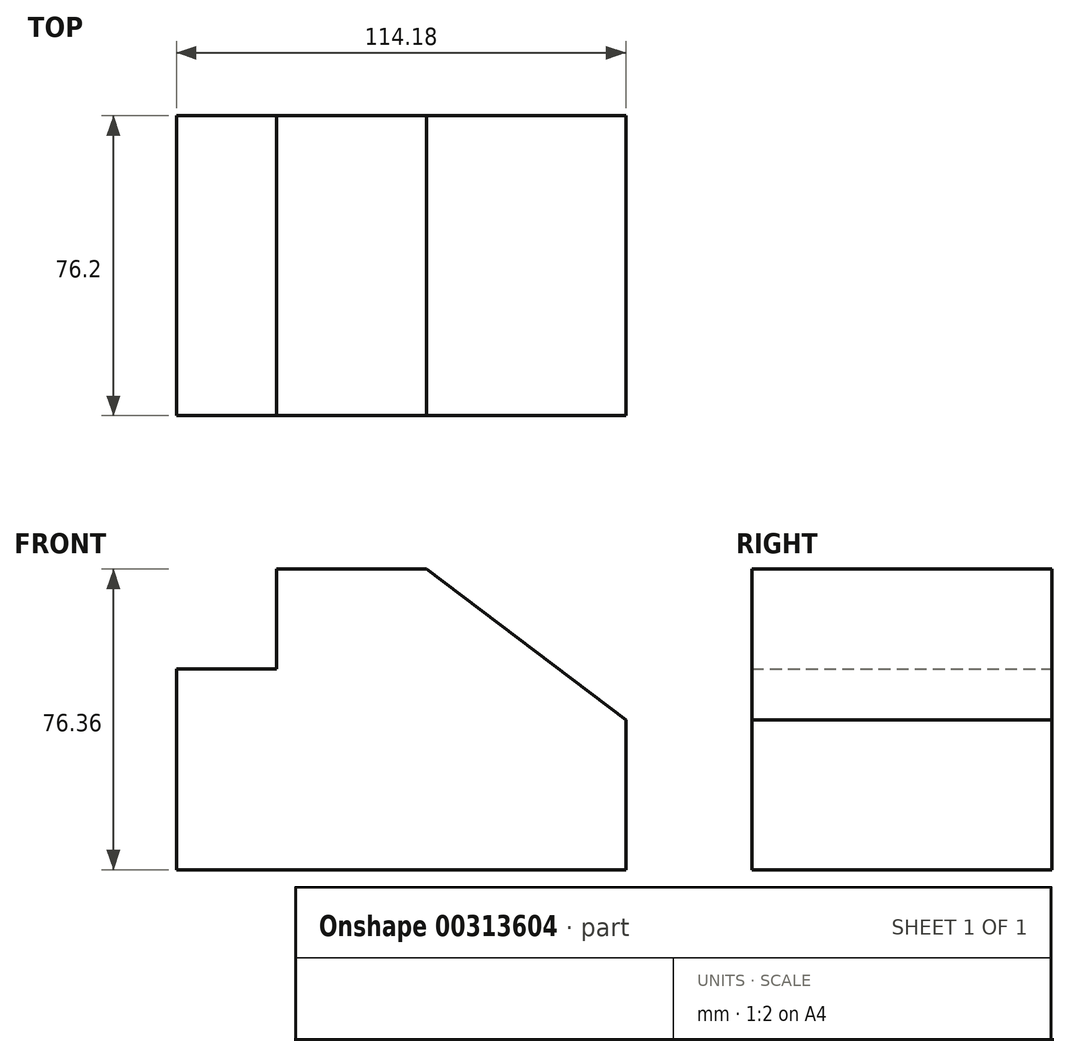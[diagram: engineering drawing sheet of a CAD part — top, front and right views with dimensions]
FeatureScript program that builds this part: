
annotation { "Feature Type Name" : "Feature", "Feature Type Description" : "" }
export const myFeature = defineFeature(function(context is Context, id is Id, definition is map)
    precondition{}
    {
        {
            var Q0;
            Q0=qCreatedBy(makeId("Front.planeOp"),FACE);
            var sketch = newSketch(context, id + "F0", { "sketchPlane" : qUnion([Q0])});
            skLineSegment(sketch, "E0", {"start": v(-38.7, -56.46) * mm, "end": v(50.2, -56.46) * mm});
            skLineSegment(sketch, "E1", {"start": v(50.2, -56.46) * mm, "end": v(50.2, -18.36) * mm});
            skLineSegment(sketch, "E2", {"start": v(50.2, -18.36) * mm, "end": v(-0.48, 19.9) * mm});
            skLineSegment(sketch, "E3", {"start": v(-0.48, 19.9) * mm, "end": v(-38.58, 19.9) * mm});
            skLineSegment(sketch, "E4", {"start": v(-38.58, 19.9) * mm, "end": v(-38.58, -5.5) * mm});
            skLineSegment(sketch, "E5", {"start": v(-63.98, -5.5) * mm, "end": v(-38.58, -5.5) * mm});
            skLineSegment(sketch, "E6", {"start": v(-63.98, -5.5) * mm, "end": v(-63.98, -45.96) * mm});
            skLineSegment(sketch, "E7", {"start": v(-63.98, -48.23) * mm, "end": v(-63.98, -56.46) * mm});
            skLineSegment(sketch, "E8", {"start": v(-63.98, -56.46) * mm, "end": v(-38.7, -56.46) * mm});
            skLineSegment(sketch, "E9", {"start": v(-63.98, -45.96) * mm, "end": v(-63.98, -48.23) * mm});
            skSolve(sketch);
        }
        {
            var Q0;
            Q0 = qSketchRegion(id + "F0", true);
            extrude(context, id + "F1", {"entities" : qUnion([Q0]), "depth" : 25.4 * mm});
        }
        {
            var Q0;
            Q0 = qSketchRegion(id + "F0", true);
            var Q1;
            Q1=makeQuery(id+"F1.opExtrude","CAP_FACE",FACE,{"disambiguationData":[OSD([sQuery(id+"F0.wireOp",EDGE,"E0"),sQuery(id+"F0.wireOp",EDGE,"E1"),sQuery(id+"F0.wireOp",EDGE,"E2"),sQuery(id+"F0.wireOp",EDGE,"E3"),sQuery(id+"F0.wireOp",EDGE,"E4"),sQuery(id+"F0.wireOp",EDGE,"E5"),sQuery(id+"F0.wireOp",EDGE,"E6"),sQuery(id+"F0.wireOp",EDGE,"E7"),sQuery(id+"F0.wireOp",EDGE,"E8"),sQuery(id+"F0.wireOp",EDGE,"E9")])],"isStart":false});
            extrude(context, id + "F2", {"entities" : qUnion([Q0, Q1]), "operationType" : NewBodyOperationType.ADD, "depth" : 50.8 * mm});
        }
    });
